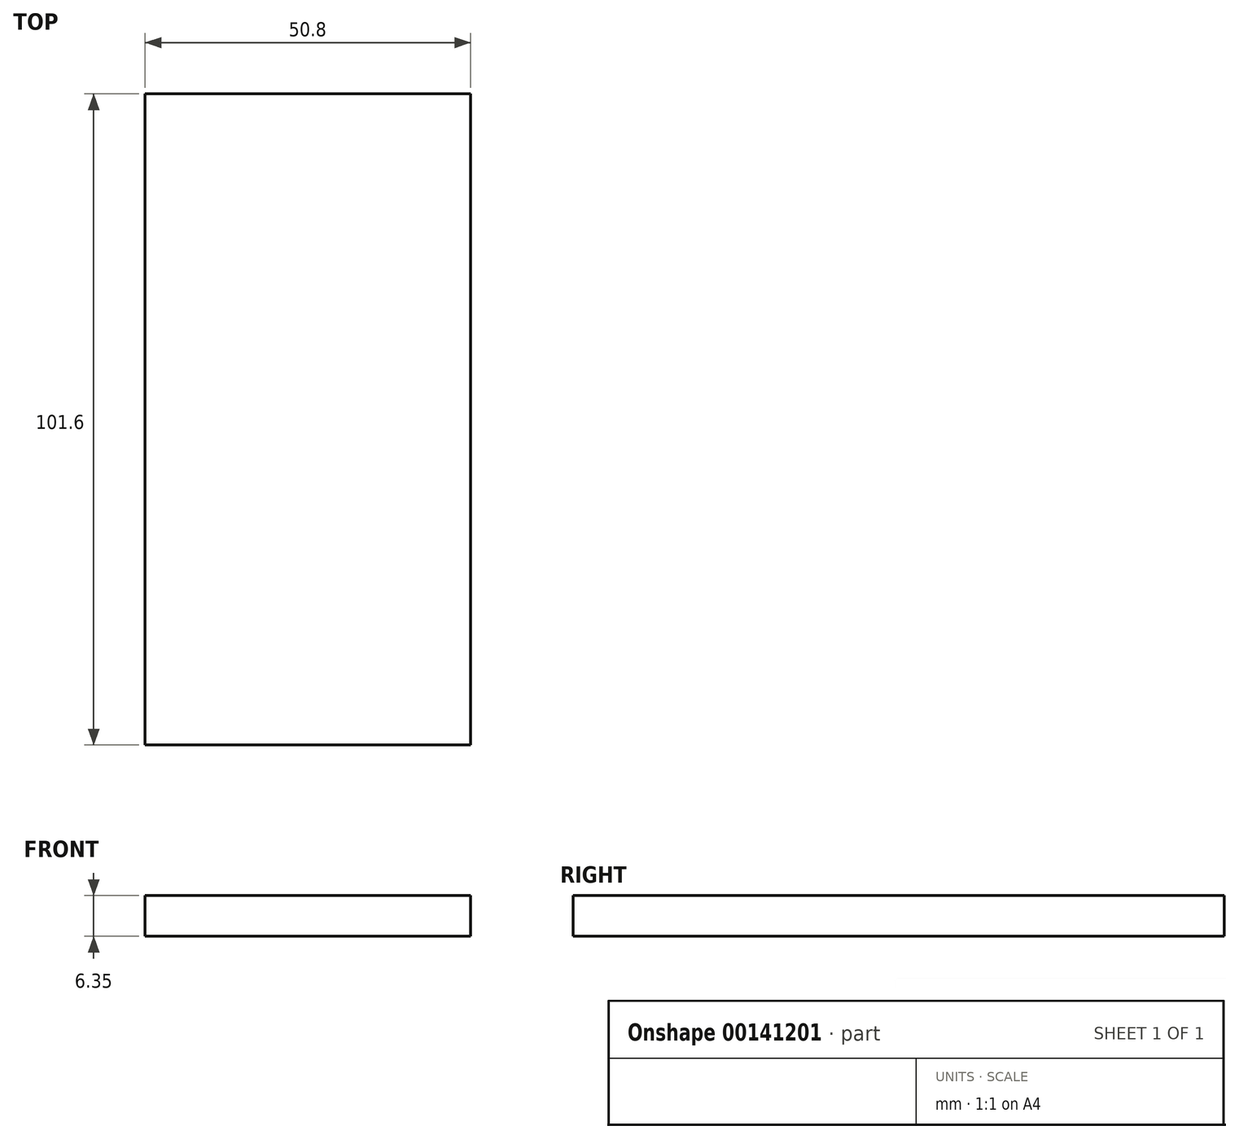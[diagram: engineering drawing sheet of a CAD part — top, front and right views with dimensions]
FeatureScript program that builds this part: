
annotation { "Feature Type Name" : "Feature", "Feature Type Description" : "" }
export const myFeature = defineFeature(function(context is Context, id is Id, definition is map)
    precondition{}
    {
        {
            var Q0;
            Q0=qCreatedBy(makeId("Top.planeOp"),FACE);
            var sketch = newSketch(context, id + "F0", { "sketchPlane" : qUnion([Q0])});
            skLineSegment(sketch, "E0.bottom", {"start": v(-24.9, 31.13) * mm, "end": v(25.9, 31.13) * mm});
            skLineSegment(sketch, "E0.top", {"start": v(-24.9, -70.47) * mm, "end": v(25.9, -70.47) * mm});
            skLineSegment(sketch, "E0.left", {"start": v(-24.9, 31.13) * mm, "end": v(-24.9, -70.47) * mm});
            skLineSegment(sketch, "E0.right", {"start": v(25.9, 31.13) * mm, "end": v(25.9, -70.47) * mm});
            skSolve(sketch);
        }
        {
            var Q0;
            Q0=makeQuery(id+"F0.imprint","IMPRINT",FACE,{"disambiguationData":[TD([[makeQuery(id+"F0.imprint","IMPRINT",EDGE,{"derivedFrom":sQuery(id+"F0.wireOp",EDGE,"E0.bottom")}),-1.0]])]});
            extrude(context, id + "F1", {"entities" : qUnion([Q0]), "depth" : 6.35 * mm});
        }
    });
